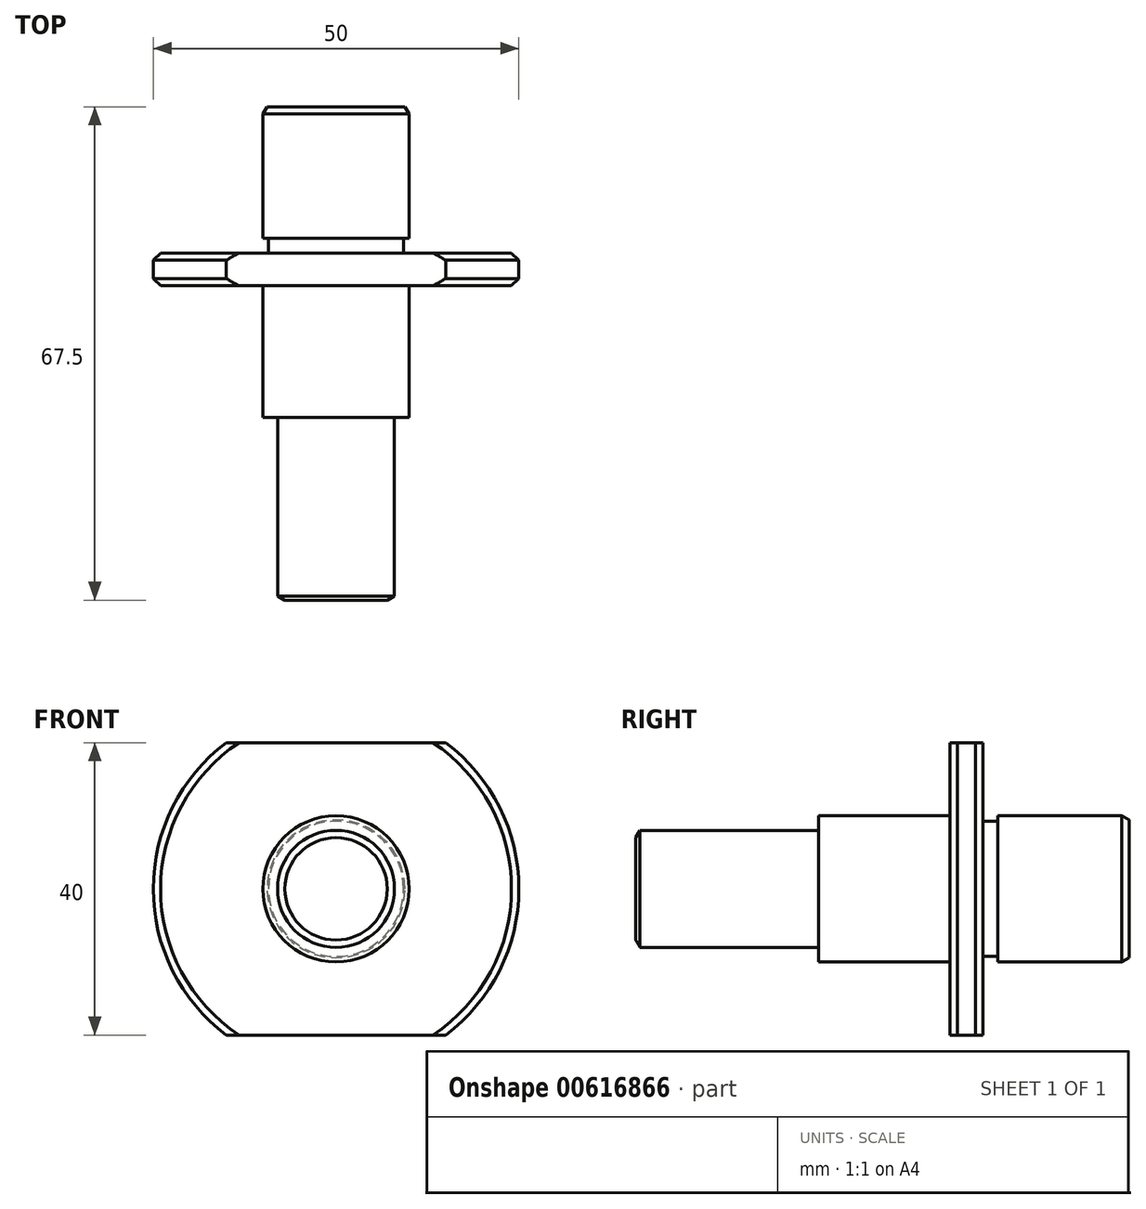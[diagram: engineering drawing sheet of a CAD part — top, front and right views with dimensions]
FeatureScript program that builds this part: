
annotation { "Feature Type Name" : "Feature", "Feature Type Description" : "" }
export const myFeature = defineFeature(function(context is Context, id is Id, definition is map)
    precondition{}
    {
        {
            var Q0;
            Q0=qCreatedBy(makeId("Right.planeOp"),FACE);
            var sketch = newSketch(context, id + "F0", { "sketchPlane" : qUnion([Q0])});
            skLineSegment(sketch, "E0", {"start": v(0, 0) * mm, "end": v(0, -8) * mm});
            skLineSegment(sketch, "E1", {"start": v(0, -8) * mm, "end": v(25, -8) * mm});
            skLineSegment(sketch, "E2", {"start": v(25, -8) * mm, "end": v(25, -10) * mm});
            skLineSegment(sketch, "E3", {"start": v(25, -10) * mm, "end": v(43, -10) * mm});
            skLineSegment(sketch, "E4", {"start": v(43, -10) * mm, "end": v(43, -25) * mm});
            skLineSegment(sketch, "E5", {"start": v(43, -25) * mm, "end": v(47.5, -25) * mm});
            skLineSegment(sketch, "E6", {"start": v(47.5, -25) * mm, "end": v(47.5, -10) * mm});
            skLineSegment(sketch, "E7", {"start": v(47.5, -10) * mm, "end": v(67.5, -10) * mm});
            skLineSegment(sketch, "E8", {"start": v(67.5, -10) * mm, "end": v(67.5, 0) * mm});
            skLineSegment(sketch, "E9", {"start": v(67.5, 0) * mm, "end": v(0, 0) * mm});
            skLineSegment(sketch, "E10", {"start": v(-68.98, 0) * mm, "end": v(144.58, 0) * mm, "construction": true});
            skSolve(sketch);
        }
        {
            var Q0;
            Q0=makeQuery(id+"F0.imprint","IMPRINT",FACE,{"disambiguationData":[TD([[makeQuery(id+"F0.imprint","IMPRINT",EDGE,{"derivedFrom":sQuery(id+"F0.wireOp",EDGE,"E0")}),1.0]])]});
            var Q1;
            Q1=sQuery(id+"F0.wireOp",EDGE,"E10");
            revolve(context, id + "F1", {"surfaceOperationType" : NewSurfaceOperationType.NEW, "entities" : qUnion([Q0]), "axis" : qUnion([Q1]), "revolveType" : RevolveType.FULL});
        }
        {
            var Q0;
            Q0=qCreatedBy(makeId("Front.planeOp"),FACE);
            var sketch = newSketch(context, id + "F2", { "sketchPlane" : qUnion([Q0])});
            skLineSegment(sketch, "E11.bottom", {"start": v(30, -20) * mm, "end": v(-30, -20) * mm});
            skLineSegment(sketch, "E11.top", {"start": v(30, -30) * mm, "end": v(-30, -30) * mm});
            skLineSegment(sketch, "E11.left", {"start": v(30, -20) * mm, "end": v(30, -30) * mm});
            skLineSegment(sketch, "E11.right", {"start": v(-30, -20) * mm, "end": v(-30, -30) * mm});
            skLineSegment(sketch, "E12.MirrorCS", {"start": v(30, 20) * mm, "end": v(-30, 20) * mm});
            skLineSegment(sketch, "E13.MirrorCS", {"start": v(-30, 20) * mm, "end": v(-30, 30) * mm});
            skLineSegment(sketch, "E14.MirrorCS", {"start": v(30, 30) * mm, "end": v(-30, 30) * mm});
            skLineSegment(sketch, "E15.MirrorCS", {"start": v(30, 20) * mm, "end": v(30, 30) * mm});
            skSolve(sketch);
        }
        {
            var Q0;
            Q0=qSketchRegion(id+"F2",true);
            extrude(context, id + "F3", {"entities" : qUnion([Q0]), "operationType" : NewBodyOperationType.REMOVE, "endBound" : BoundingType.THROUGH_ALL, "oppositeDirection" : true, "depth" : 25 * mm, "offsetDistance" : 25 * mm});
        }
        {
            var Q0;
            Q0=makeQuery(id+"F1.opRevolve","SWEPT_EDGE",EDGE,{"disambiguationData":[OSD([sQuery(id+"F0.wireOp",EDGE,"E5"),sQuery(id+"F0.wireOp",EDGE,"E6")])]});
            var Q1;
            Q1=makeQuery(id+"F1.opRevolve","SWEPT_EDGE",EDGE,{"disambiguationData":[OSD([sQuery(id+"F0.wireOp",EDGE,"E4"),sQuery(id+"F0.wireOp",EDGE,"E5")])]});
            chamfer(context, id + "F4", {"entities" : qUnion([Q0, Q1]), "width" : 1 * mm, "tangentPropagation" : true});
        }
        {
            var Q0;
            Q0=makeQuery(id+"F1.opRevolve","SWEPT_EDGE",EDGE,{"disambiguationData":[OSD([sQuery(id+"F0.wireOp",EDGE,"E0"),sQuery(id+"F0.wireOp",EDGE,"E1")])]});
            var Q1;
            Q1=makeQuery(id+"F1.opRevolve","SWEPT_EDGE",EDGE,{"disambiguationData":[OSD([sQuery(id+"F0.wireOp",EDGE,"E7"),sQuery(id+"F0.wireOp",EDGE,"E8")])]});
            chamfer(context, id + "F5", {"entities" : qUnion([Q0, Q1]), "chamferType" : ChamferType.OFFSET_ANGLE, "width" : 1 * mm, "oppositeDirection" : false, "angle" : 30 * degree, "tangentPropagation" : true});
        }
        {
            var Q0;
            Q0=qCreatedBy(makeId("Right.planeOp"),FACE);
            var sketch = newSketch(context, id + "F6", { "sketchPlane" : qUnion([Q0])});
            skLineSegment(sketch, "E16", {"start": v(47.5, 9.25) * mm, "end": v(47.5, 11.25) * mm});
            skLineSegment(sketch, "E17", {"start": v(47.5, 11.25) * mm, "end": v(49.5, 11.25) * mm});
            skLineSegment(sketch, "E18", {"start": v(49.5, 11.25) * mm, "end": v(49.5, 9.25) * mm});
            skLineSegment(sketch, "E19", {"start": v(47.5, 10) * mm, "end": v(91.5, 10) * mm, "construction": true});
            skLineSegment(sketch, "E20", {"start": v(47.5, 9.25) * mm, "end": v(49.5, 9.25) * mm});
            skLineSegment(sketch, "E21", {"start": v(77.36, 0) * mm, "end": v(55.72, 0) * mm, "construction": true});
            skSolve(sketch);
        }
        {
            var Q0;
            Q0=makeQuery(id+"F6.imprint","IMPRINT",FACE,{"disambiguationData":[TD([[makeQuery(id+"F6.imprint","IMPRINT",EDGE,{"derivedFrom":sQuery(id+"F6.wireOp",EDGE,"E16")}),-1.0]])]});
            var Q1;
            Q1=sQuery(id+"F6.wireOp",EDGE,"E21");
            revolve(context, id + "F7", {"operationType" : NewBodyOperationType.REMOVE, "surfaceOperationType" : NewSurfaceOperationType.NEW, "entities" : qUnion([Q0]), "axis" : qUnion([Q1]), "revolveType" : RevolveType.FULL, "oppositeDirection" : true});
        }
    });
